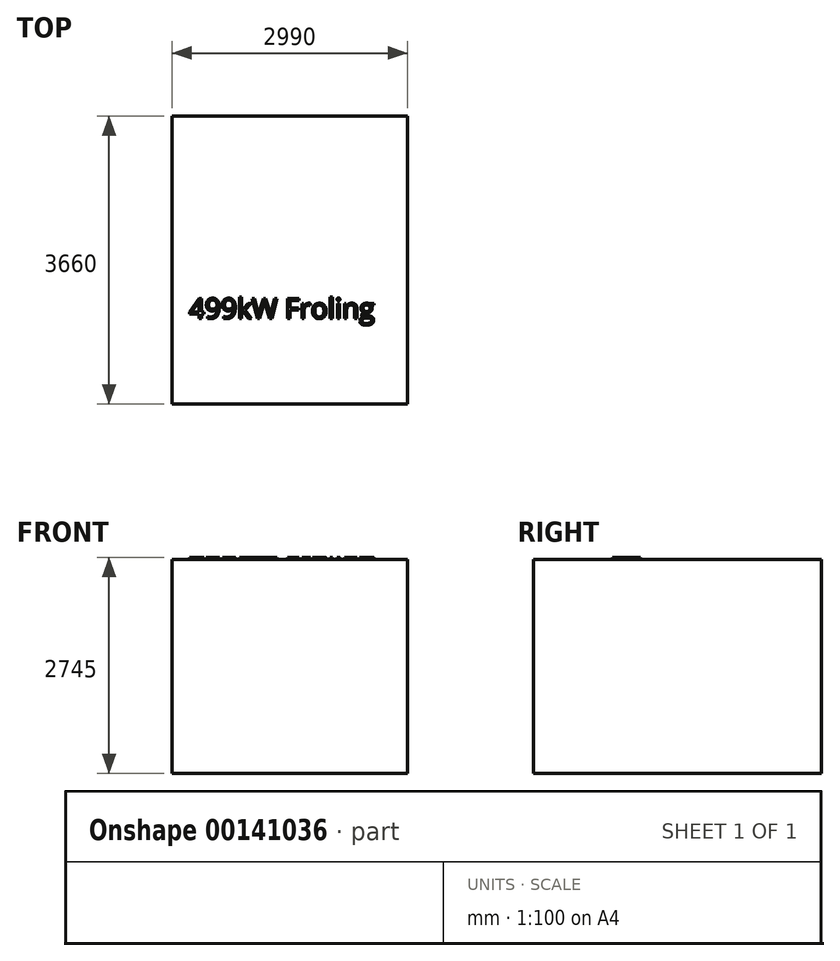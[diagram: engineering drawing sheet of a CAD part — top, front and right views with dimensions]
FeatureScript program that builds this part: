
annotation { "Feature Type Name" : "Feature", "Feature Type Description" : "" }
export const myFeature = defineFeature(function(context is Context, id is Id, definition is map)
    precondition{}
    {
        {
            var Q0;
            Q0=qCreatedBy(makeId("Top.planeOp"),FACE);
            var sketch = newSketch(context, id + "F0", { "sketchPlane" : qUnion([Q0])});
            skLineSegment(sketch, "E0.bottom", {"start": v(0, 0) * mm, "end": v(2990, 0) * mm});
            skLineSegment(sketch, "E0.top", {"start": v(0, 3660) * mm, "end": v(2990, 3660) * mm});
            skLineSegment(sketch, "E0.left", {"start": v(0, 0) * mm, "end": v(0, 3660) * mm});
            skLineSegment(sketch, "E0.right", {"start": v(2990, 0) * mm, "end": v(2990, 3660) * mm});
            skSolve(sketch);
        }
        {
            var Q0;
            Q0=qSketchRegion(id+"F0",true);
            extrude(context, id + "F1", {"entities" : qUnion([Q0]), "depth" : 2720 * mm});
        }
        {
            var Q0;
            Q0=makeQuery(id+"F1.opExtrude","CAP_FACE",FACE,{"disambiguationData":[OSD([sQuery(id+"F0.wireOp",EDGE,"E0.bottom"),sQuery(id+"F0.wireOp",EDGE,"E0.top"),sQuery(id+"F0.wireOp",EDGE,"E0.left"),sQuery(id+"F0.wireOp",EDGE,"E0.right")])],"isStart":false});
            var sketch = newSketch(context, id + "F2", { "sketchPlane" : qUnion([Q0])});
            skText(sketch, "E1", { "text": "499kW Froling", "fontName": "OpenSans-Regular.ttf"});
            const initialGuessF2  = {"E1": [0.21266, 1.0867, 1, 0, 0.2566]};
            skSetInitialGuess(sketch, initialGuessF2);
            skSolve(sketch);
        }
        {
            var Q0;
            Q0=qSketchRegion(id+"F2",true);
            extrude(context, id + "F3", {"entities" : qUnion([Q0]), "operationType" : NewBodyOperationType.ADD, "depth" : 25 * mm});
        }
    });
